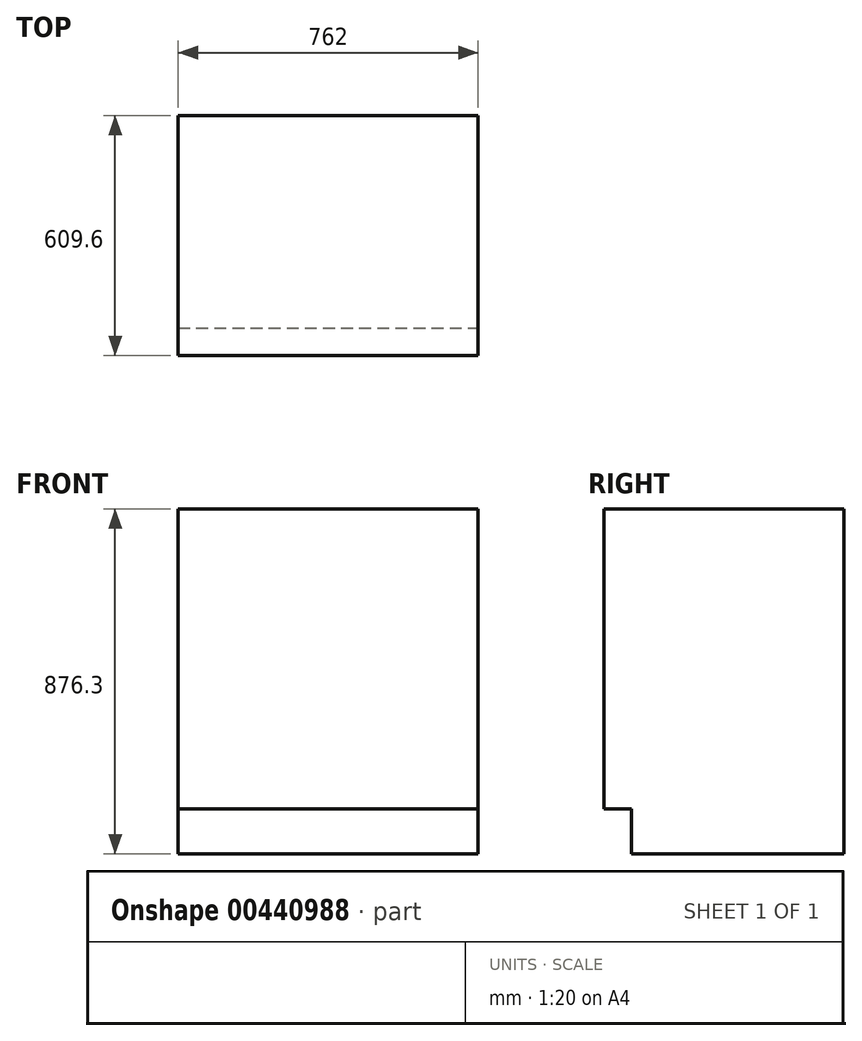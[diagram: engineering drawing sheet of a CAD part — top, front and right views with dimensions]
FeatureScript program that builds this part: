
annotation { "Feature Type Name" : "Feature", "Feature Type Description" : "" }
export const myFeature = defineFeature(function(context is Context, id is Id, definition is map)
    precondition{}
    {
        {
            var Q0;
            Q0=qCreatedBy(makeId("Front.planeOp"),FACE);
            var sketch = newSketch(context, id + "F0", { "sketchPlane" : qUnion([Q0])});
            skLineSegment(sketch, "E0.bottom", {"start": v(0, 0) * mm, "end": v(762, 0) * mm});
            skLineSegment(sketch, "E0.top", {"start": v(0, 876.3) * mm, "end": v(762, 876.3) * mm});
            skLineSegment(sketch, "E0.left", {"start": v(0, 0) * mm, "end": v(0, 876.3) * mm});
            skLineSegment(sketch, "E0.right", {"start": v(762, 0) * mm, "end": v(762, 876.3) * mm});
            skSolve(sketch);
        }
        {
            var Q0;
            Q0=makeQuery(id+"F0.imprint","IMPRINT",FACE,{"disambiguationData":[TD([[makeQuery(id+"F0.imprint","IMPRINT",EDGE,{"derivedFrom":sQuery(id+"F0.wireOp",EDGE,"E0.bottom")}),1.0]])]});
            extrude(context, id + "F1", {"entities" : qUnion([Q0]), "oppositeDirection" : true, "depth" : 609.6 * mm});
        }
        {
            var Q0;
            Q0=makeQuery(id+"F1.opExtrude","CAP_FACE",FACE,{"disambiguationData":[OSD([sQuery(id+"F0.wireOp",EDGE,"E0.bottom"),sQuery(id+"F0.wireOp",EDGE,"E0.top"),sQuery(id+"F0.wireOp",EDGE,"E0.left"),sQuery(id+"F0.wireOp",EDGE,"E0.right")])],"isStart":true});
            var sketch = newSketch(context, id + "F2", { "sketchPlane" : qUnion([Q0])});
            skLineSegment(sketch, "E1.bottom", {"start": v(0, 0) * mm, "end": v(762, 0) * mm});
            skLineSegment(sketch, "E1.top", {"start": v(0, 114.3) * mm, "end": v(762, 114.3) * mm});
            skLineSegment(sketch, "E1.left", {"start": v(0, 0) * mm, "end": v(0, 114.3) * mm});
            skLineSegment(sketch, "E1.right", {"start": v(762, 0) * mm, "end": v(762, 114.3) * mm});
            skSolve(sketch);
        }
        {
            var Q0;
            Q0=makeQuery(id+"F2.imprint","IMPRINT",FACE,{"disambiguationData":[TD([[makeQuery(id+"F2.imprint","IMPRINT",EDGE,{"derivedFrom":sQuery(id+"F2.wireOp",EDGE,"E1.bottom")}),1.0]])]});
            extrude(context, id + "F3", {"entities" : qUnion([Q0]), "operationType" : NewBodyOperationType.REMOVE, "oppositeDirection" : true, "depth" : 69.85 * mm});
        }
    });
